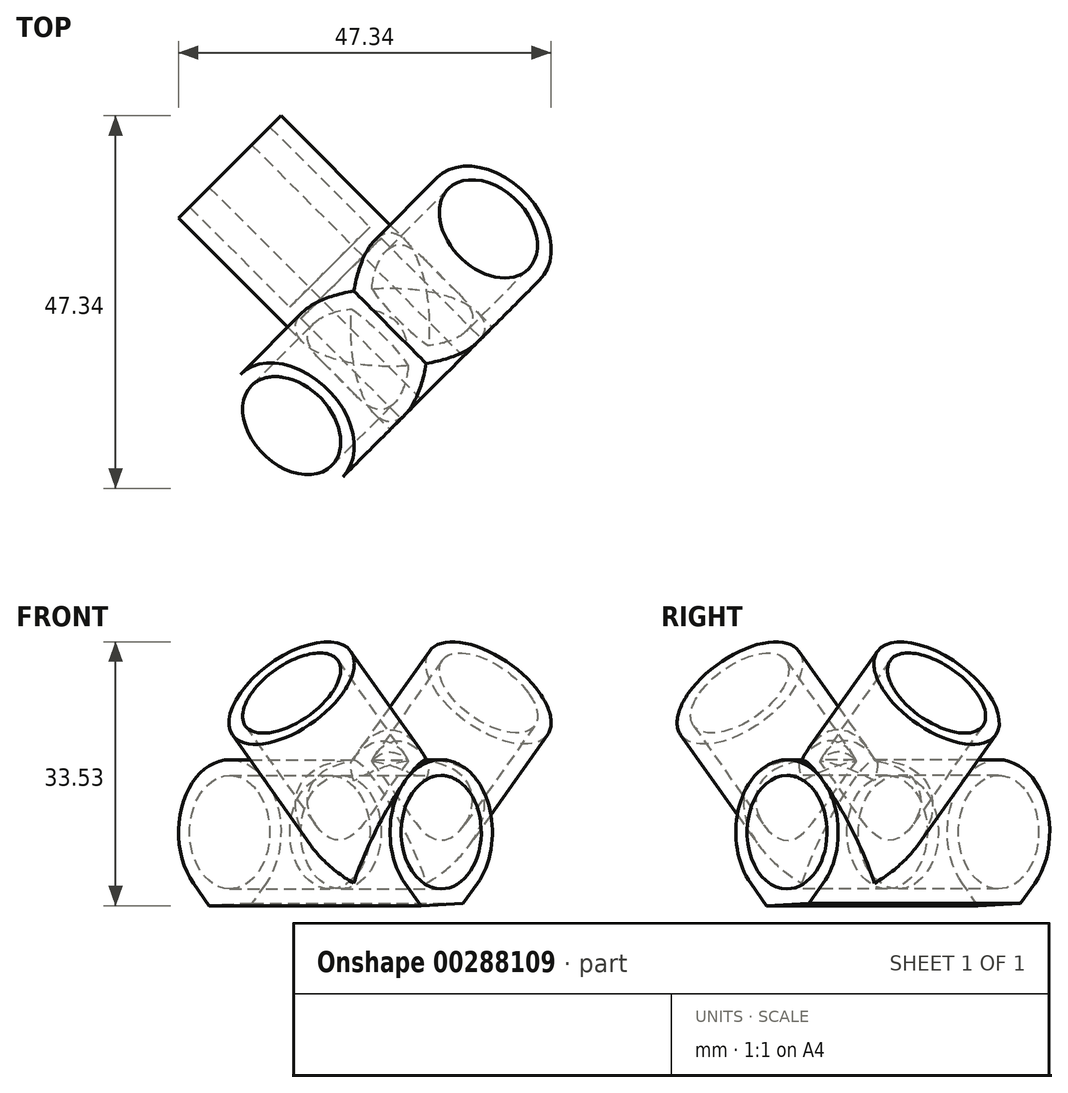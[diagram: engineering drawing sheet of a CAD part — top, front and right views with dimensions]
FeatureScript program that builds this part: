
annotation { "Feature Type Name" : "Feature", "Feature Type Description" : "" }
export const myFeature = defineFeature(function(context is Context, id is Id, definition is map)
    precondition{}
    {
        {
            var Q0;
            Q0=qCreatedBy(makeId("Front.planeOp"),FACE);
            var sketch = newSketch(context, id + "F0", { "sketchPlane" : qUnion([Q0])});
            skLineSegment(sketch, "E0", {"start": v(0, 9.2) * mm, "end": v(0, 0) * mm, "construction": true});
            skCircle(sketch, "E1", {"center": v(0, 9.2) * mm, "radius": 7.2 * mm});
            skCircle(sketch, "E2.0", {"center": v(0, 9.2) * mm, "radius": 9.2 * mm});
            skSolve(sketch);
        }
        {
            var Q0;
            Q0=makeQuery(id+"F0.imprint","IMPRINT",FACE,{"disambiguationData":[TD([[makeQuery(id+"F0.imprint","IMPRINT",EDGE,{"derivedFrom":sQuery(id+"F0.wireOp",EDGE,"E1")}),-1.0]])]});
            extrude(context, id + "F1", {"entities" : qUnion([Q0]), "depth" : 25 * mm});
        }
        {
            var Q0;
            Q0=qCreatedBy(makeId("Right.planeOp"),FACE);
            var sketch = newSketch(context, id + "F2", { "sketchPlane" : qUnion([Q0])});
            skLineSegment(sketch, "E3", {"start": v(0, 9.2) * mm, "end": v(0, 0) * mm, "construction": true});
            skCircle(sketch, "E4", {"center": v(0, 9.2) * mm, "radius": 7.2 * mm});
            skCircle(sketch, "E5.0", {"center": v(0, 9.2) * mm, "radius": 9.2 * mm});
            skSolve(sketch);
        }
        {
            var Q0;
            {var subQ0=sQuery(id+"F4.wireOp",EDGE,"E8.bottom");var subQ1=sQuery(id+"F4.wireOp",EDGE,"E7.0");var subQ2=makeQuery(id+"F4.imprint","INTERSECT",VERTEX,{"derivedFrom":[subQ1,subQ0]});Q0=makeQuery(id+"F4.imprint","IMPRINT",FACE,{"disambiguationData":[TD([[makeQuery(id+"F4.imprint","IMPRINT",EDGE,{"disambiguationData":[TD([[subQ2,1.0]])],"derivedFrom":subQ1}),-1.0]])]});}
            var Q1;
            Q1=makeQuery(id+"F2.imprint","IMPRINT",FACE,{"disambiguationData":[TD([[makeQuery(id+"F2.imprint","IMPRINT",EDGE,{"derivedFrom":sQuery(id+"F2.wireOp",EDGE,"E4")}),-1.0]])]});
            extrude(context, id + "F3", {"entities" : qUnion([Q0, Q1]), "depth" : 25 * mm});
        }
        {
            var Q0;
            Q0=qCreatedBy(makeId("Top.planeOp"),FACE);
            var sketch = newSketch(context, id + "F4", { "sketchPlane" : qUnion([Q0])});
            skCircle(sketch, "E6", {"center": v(0, 0) * mm, "radius": 7.2 * mm});
            skCircle(sketch, "E7.0", {"center": v(0, 0) * mm, "radius": 9.2 * mm});
            skLineSegment(sketch, "E8.bottom", {"start": v(9.2, 9.2) * mm, "end": v(-9.2, 9.2) * mm});
            skLineSegment(sketch, "E8.top", {"start": v(9.2, -9.2) * mm, "end": v(-9.2, -9.2) * mm});
            skLineSegment(sketch, "E8.left", {"start": v(9.2, 9.2) * mm, "end": v(9.2, -9.2) * mm});
            skLineSegment(sketch, "E8.right", {"start": v(-9.2, 9.2) * mm, "end": v(-9.2, -9.2) * mm});
            skLineSegment(sketch, "E9", {"start": v(-9.2, -9.2) * mm, "end": v(9.2, 9.2) * mm, "construction": true});
            skPoint(sketch, "E10", {"position": v(-9.2, 0) * mm});
            skLineSegment(sketch, "E11", {"start": v(-3.6, 9.2) * mm, "end": v(-9.2, 4.02) * mm});
            skSolve(sketch);
        }
        {
            var Q0;
            {var subQ0=sQuery(id+"F4.wireOp",EDGE,"E8.right");var subQ1=sQuery(id+"F4.wireOp",EDGE,"E7.0");var subQ2=makeQuery(id+"F4.imprint","INTERSECT",VERTEX,{"derivedFrom":[subQ1,subQ0]});Q0=makeQuery(id+"F4.imprint","IMPRINT",FACE,{"disambiguationData":[TD([[makeQuery(id+"F4.imprint","IMPRINT",EDGE,{"disambiguationData":[TD([[subQ2,1.0]])],"derivedFrom":subQ1}),-1.0]])]});}
            var Q1;
            {var subQ0=sQuery(id+"F4.wireOp",EDGE,"E8.bottom");var subQ1=sQuery(id+"F4.wireOp",EDGE,"E7.0");var subQ2=makeQuery(id+"F4.imprint","INTERSECT",VERTEX,{"derivedFrom":[subQ1,subQ0]});Q1=makeQuery(id+"F4.imprint","IMPRINT",FACE,{"disambiguationData":[TD([[makeQuery(id+"F4.imprint","IMPRINT",EDGE,{"disambiguationData":[TD([[subQ2,-1.0]])],"derivedFrom":subQ1}),-1.0]])]});}
            var Q2;
            Q2=makeQuery(id+"F4.imprint","IMPRINT",FACE,{"disambiguationData":[TD([[makeQuery(id+"F4.imprint","IMPRINT",EDGE,{"derivedFrom":sQuery(id+"F4.wireOp",EDGE,"E6")}),-1.0]])]});
            extrude(context, id + "F5", {"entities" : qUnion([Q0, Q1, Q2]), "operationType" : NewBodyOperationType.ADD, "depth" : 38 * mm});
        }
        {
            var Q0;
            Q0=makeQuery(id+"F4.imprint","IMPRINT",FACE,{"disambiguationData":[TD([[makeQuery(id+"F4.imprint","IMPRINT",EDGE,{"derivedFrom":sQuery(id+"F4.wireOp",EDGE,"E6")}),1.0]])]});
            extrude(context, id + "F6", {"entities" : qUnion([Q0]), "operationType" : NewBodyOperationType.REMOVE, "depth" : 25 * mm});
        }
        {
            var Q0;
            Q0=makeQuery(id+"F4.imprint","IMPRINT",FACE,{"disambiguationData":[TD([[makeQuery(id+"F4.imprint","IMPRINT",EDGE,{"derivedFrom":sQuery(id+"F4.wireOp",EDGE,"E6")}),1.0]])]});
            extrude(context, id + "F7", {"entities" : qUnion([Q0]), "operationType" : NewBodyOperationType.ADD, "depth" : 20 * mm, "hasSecondDirection" : true, "secondDirectionOppositeDirection" : false, "secondDirectionDepth" : 18 * mm});
        }
        {
            var Q0;
            Q0=makeQuery(id+"F1.opExtrude","SWEPT_BODY",BODY,{"disambiguationData":[OSD([sQuery(id+"F0.wireOp",EDGE,"E1"),sQuery(id+"F0.wireOp",EDGE,"E2.0")])]});
            var Q1;
            Q1=sQuery(id+"F4.wireOp",EDGE,"E9");
            transform(context, id + "F8", {"entities" : qUnion([Q0]), "transformType" : TransformType.ROTATION, "transformAxis" : qUnion([Q1]), "angle" : 90 * degree, "oppositeDirection" : true, "makeCopy" : false});
        }
    });
